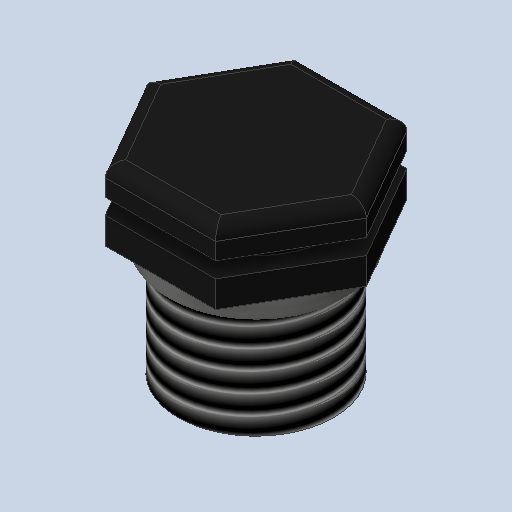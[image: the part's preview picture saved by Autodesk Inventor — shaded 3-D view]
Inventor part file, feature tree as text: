
AUTODESK INVENTOR PART (.ipt)
format: ipt  version: 2024.2 (Build 282272000, 272)  size: 250,368 bytes
history: native  units: mm
features: revolve x2, extrude x2, thread x1, plane x1, fillet x1, sketch x1, projected_geometry x1
ambient origin geometry x8: Origin, YZ Plane, XZ Plane, XY Plane, X Axis, Y Axis, Z Axis, Center Point
bodies: Solid1 (feature_tree), Solid2 (feature_tree)
feature tree (9):
  revolve  "Revolution1"  [1 undecoded]
  thread  "Thread1"  [1 undecoded]
  revolve  "Revolution2"  [1 undecoded]
  extrude  "Extrusion1"  TaperAngle=90.0deg  [1 undecoded]
  plane  "Work Plane1"
  extrude  "Extrusion2"  Depth=10.0mm TaperAngle=0.0deg
  fillet  "Fillet2"  Radius=2.0mm
  sketch  "Sketch4"  dims[d0=10.0mm d1=5.55mm d2=8.5mm d3=6.0mm d4=90.0deg d6=10.0mm d7=0.0mm d8=2.0mm d9=90.0deg d10=10.0mm d11=0.0mm d12=-3.5mm d13=1.2mm d14=0.0mm d15=1.0mm]
  projected_geometry  "Projected Loop1"
note: 4 required parameter values undecoded (feature->parameter linkage not recoverable at this tier; creation-order binding heuristic only, values carry confidence <= 0.55)